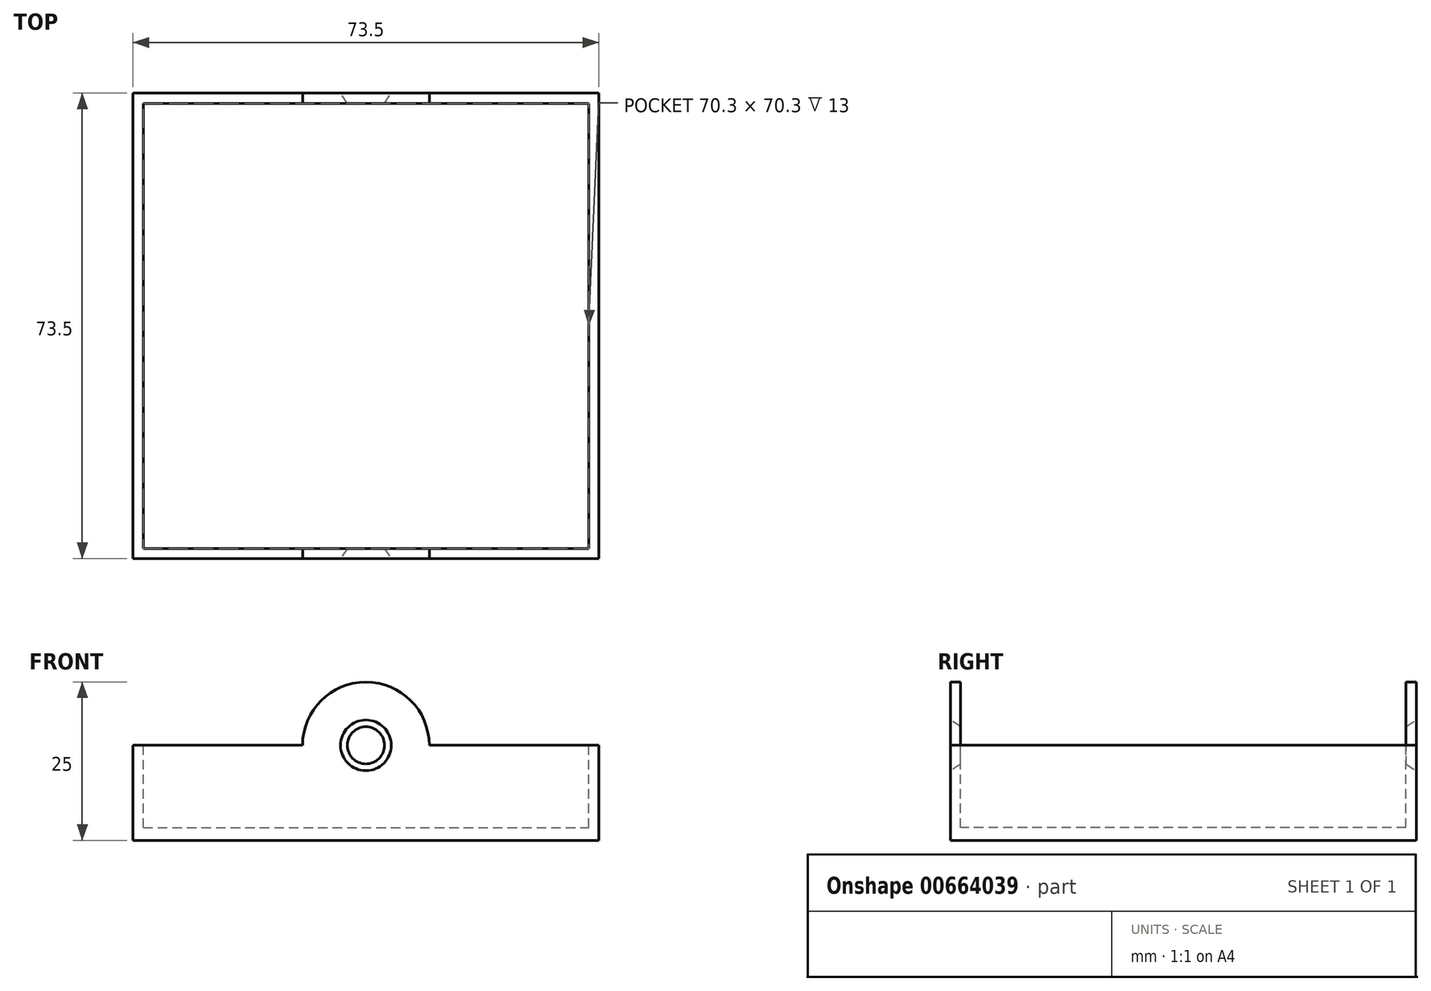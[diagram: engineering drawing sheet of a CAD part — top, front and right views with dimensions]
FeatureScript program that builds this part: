
annotation { "Feature Type Name" : "Feature", "Feature Type Description" : "" }
export const myFeature = defineFeature(function(context is Context, id is Id, definition is map)
    precondition{}
    {
        {
            var Q0;
            Q0=qCreatedBy(makeId("Front.planeOp"),FACE);
            var sketch = newSketch(context, id + "F0", { "sketchPlane" : qUnion([Q0])});
            skLineSegment(sketch, "E0.bottom", {"start": v(0, 0) * mm, "end": v(73.5, 0) * mm});
            skLineSegment(sketch, "E0.top", {"start": v(0, 25) * mm, "end": v(73.5, 25) * mm});
            skLineSegment(sketch, "E0.left", {"start": v(0, 0) * mm, "end": v(0, 25) * mm});
            skLineSegment(sketch, "E0.right", {"start": v(73.5, 0) * mm, "end": v(73.5, 25) * mm});
            skLineSegment(sketch, "E1", {"start": v(0, 15) * mm, "end": v(73.5, 15) * mm});
            skPoint(sketch, "E2", {"position": v(36.75, 25) * mm});
            skArc(sketch, "E3", {"start": v(46.75, 15) * mm, "mid": v(36.75, 25) * mm, "end": v(26.75, 15) * mm});
            skCircle(sketch, "E4", {"center": v(36.75, 15) * mm, "radius": 2 * mm});
            skSolve(sketch);
        }
        {
            var Q0;
            Q0 = qSketchRegion(id + "F0", true);
            extrude(context, id + "F1", {"entities" : qUnion([Q0]), "oppositeDirection" : true, "depth" : 73.5 * mm, "offsetDistance" : 25 * mm});
        }
        {
            var Q0;
            Q0=makeQuery(id+"F1.opExtrude","SWEPT_FACE",FACE,{"disambiguationData":[OSD([sQuery(id+"F0.wireOp",EDGE,"E0.top")])]});
            var sketch = newSketch(context, id + "F2", { "sketchPlane" : qUnion([Q0])});
            skLineSegment(sketch, "E5.0", {"start": v(1.6, 1.6) * mm, "end": v(71.9, 1.6) * mm});
            skLineSegment(sketch, "E5.1", {"start": v(1.6, 71.9) * mm, "end": v(1.6, 1.6) * mm});
            skLineSegment(sketch, "E5.2", {"start": v(71.9, 71.9) * mm, "end": v(1.6, 71.9) * mm});
            skLineSegment(sketch, "E5.3", {"start": v(71.9, 1.6) * mm, "end": v(71.9, 71.9) * mm});
            skSolve(sketch);
        }
        {
            var Q0;
            Q0=makeQuery(id+"F2.imprint","IMPRINT",FACE,{"disambiguationData":[TD([[makeQuery(id+"F2.imprint","IMPRINT",EDGE,{"derivedFrom":sQuery(id+"F2.wireOp",EDGE,"E5.0")}),1.0]])]});
            extrude(context, id + "F3", {"entities" : qUnion([Q0]), "operationType" : NewBodyOperationType.REMOVE, "oppositeDirection" : true, "depth" : 23 * mm, "offsetDistance" : 25 * mm});
        }
        {
            var Q0;
            {var subQ0=sQuery(id+"F0.wireOp",EDGE,"E0.left");var subQ1=sQuery(id+"F0.wireOp",EDGE,"E0.top");var subQ2=makeQuery(id+"F0.imprint","INTERSECT",VERTEX,{"derivedFrom":[subQ1,subQ0]});Q0=makeQuery(id+"F0.imprint","IMPRINT",FACE,{"disambiguationData":[TD([[makeQuery(id+"F0.imprint","IMPRINT",EDGE,{"disambiguationData":[TD([[subQ2,-1.0]])],"derivedFrom":subQ1}),-1.0]])]});}
            var Q1;
            {var subQ0=sQuery(id+"F0.wireOp",EDGE,"E0.right");var subQ1=sQuery(id+"F0.wireOp",EDGE,"E0.top");var subQ2=makeQuery(id+"F0.imprint","INTERSECT",VERTEX,{"derivedFrom":[subQ1,subQ0]});Q1=makeQuery(id+"F0.imprint","IMPRINT",FACE,{"disambiguationData":[TD([[makeQuery(id+"F0.imprint","IMPRINT",EDGE,{"disambiguationData":[TD([[subQ2,1.0]])],"derivedFrom":subQ1}),-1.0]])]});}
            extrude(context, id + "F4", {"entities" : qUnion([Q0, Q1]), "operationType" : NewBodyOperationType.REMOVE, "endBound" : BoundingType.THROUGH_ALL, "oppositeDirection" : true, "depth" : 25 * mm, "offsetDistance" : 25 * mm});
        }
        {
            var Q0;
            Q0=makeQuery(id+"F1.opExtrude","CAP_EDGE",EDGE,{"disambiguationData":[OSD([sQuery(id+"F0.wireOp",EDGE,"E4")])],"isStart":true});
            chamfer(context, id + "F5", {"entities" : qUnion([Q0]), "chamferType" : ChamferType.TWO_OFFSETS, "width1" : 3 * mm, "oppositeDirection" : false, "width2" : 2 * mm, "tangentPropagation" : true});
        }
        {
            var Q0;
            Q0=makeQuery(id+"F1.opExtrude","CAP_EDGE",EDGE,{"disambiguationData":[OSD([sQuery(id+"F0.wireOp",EDGE,"E4")])],"isStart":false});
            chamfer(context, id + "F6", {"entities" : qUnion([Q0]), "chamferType" : ChamferType.TWO_OFFSETS, "width1" : 3 * mm, "oppositeDirection" : true, "width2" : 2 * mm, "tangentPropagation" : true});
        }
    });
